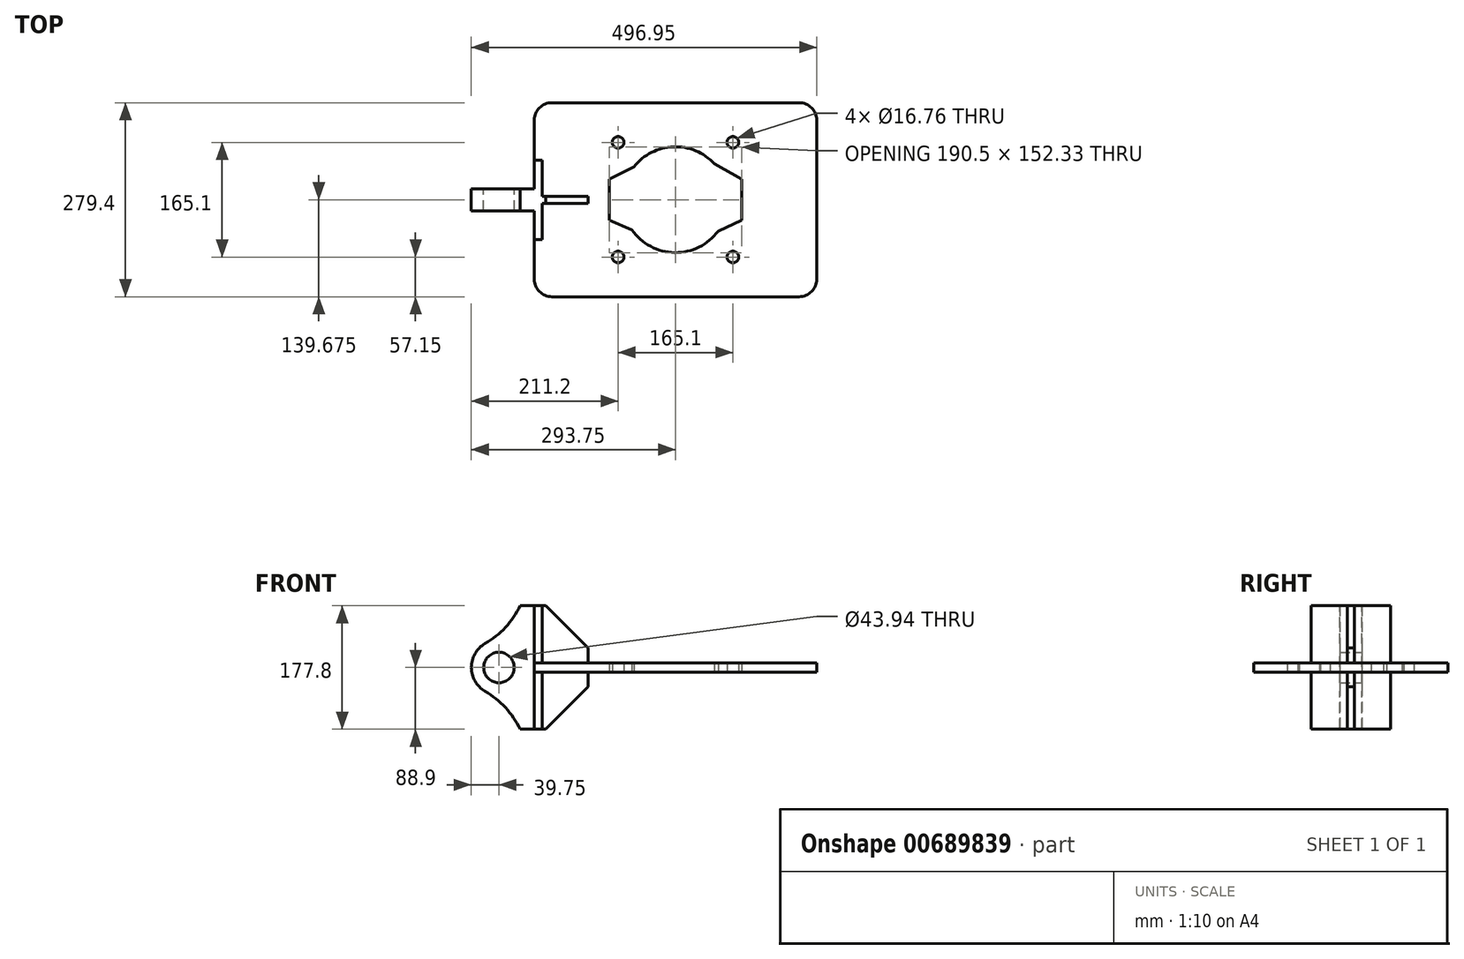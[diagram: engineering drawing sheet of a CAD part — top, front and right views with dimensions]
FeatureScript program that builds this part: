
annotation { "Feature Type Name" : "Feature", "Feature Type Description" : "" }
export const myFeature = defineFeature(function(context is Context, id is Id, definition is map)
    precondition{}
    {
        {
            var Q0;
            Q0=qCreatedBy(makeId("Top.planeOp"),FACE);
            var sketch = newSketch(context, id + "F0", { "sketchPlane" : qUnion([Q0])});
            skLineSegment(sketch, "E0.bottom", {"start": v(-177.8, 139.7) * mm, "end": v(177.8, 139.7) * mm});
            skLineSegment(sketch, "E0.top", {"start": v(-177.8, -139.7) * mm, "end": v(177.8, -139.7) * mm});
            skLineSegment(sketch, "E0.left", {"start": v(-203.2, 114.3) * mm, "end": v(-203.2, -114.3) * mm});
            skLineSegment(sketch, "E0.right", {"start": v(203.2, 114.3) * mm, "end": v(203.2, -114.3) * mm});
            skPoint(sketch, "E0.middle", {"position": v(0, 0) * mm});
            skLineSegment(sketch, "E1.bottom", {"start": v(-82.55, 82.55) * mm, "end": v(82.55, 82.55) * mm, "construction": true});
            skLineSegment(sketch, "E1.top", {"start": v(-82.55, -82.55) * mm, "end": v(82.55, -82.55) * mm, "construction": true});
            skLineSegment(sketch, "E1.left", {"start": v(-82.55, 82.55) * mm, "end": v(-82.55, -82.55) * mm, "construction": true});
            skLineSegment(sketch, "E1.right", {"start": v(82.55, 82.55) * mm, "end": v(82.55, -82.55) * mm, "construction": true});
            skCircle(sketch, "E2", {"center": v(-82.55, 82.55) * mm, "radius": 8.38 * mm});
            skCircle(sketch, "E3", {"center": v(82.55, 82.55) * mm, "radius": 8.38 * mm});
            skCircle(sketch, "E4", {"center": v(82.55, -82.55) * mm, "radius": 8.38 * mm});
            skCircle(sketch, "E5", {"center": v(-82.55, -82.55) * mm, "radius": 8.38 * mm});
            skPoint(sketch, "E6.visualSharp", {"position": v(-203.2, 139.7) * mm});
            skArc(sketch, "E6.filletArc", {"start": v(-177.8, 139.7) * mm, "mid": v(-195.76, 132.26) * mm, "end": v(-203.2, 114.3) * mm});
            skPoint(sketch, "E7.visualSharp", {"position": v(203.2, 139.7) * mm});
            skArc(sketch, "E7.filletArc", {"start": v(203.2, 114.3) * mm, "mid": v(195.76, 132.26) * mm, "end": v(177.8, 139.7) * mm});
            skPoint(sketch, "E8.visualSharp", {"position": v(-203.2, -139.7) * mm});
            skArc(sketch, "E8.filletArc", {"start": v(-203.2, -114.3) * mm, "mid": v(-195.76, -132.26) * mm, "end": v(-177.8, -139.7) * mm});
            skPoint(sketch, "E9.visualSharp", {"position": v(203.2, -139.7) * mm});
            skArc(sketch, "E9.filletArc", {"start": v(177.8, -139.7) * mm, "mid": v(195.76, -132.26) * mm, "end": v(203.2, -114.3) * mm});
            skSolve(sketch);
        }
        {
            var Q0;
            Q0 = qSketchRegion(id + "F0", true);
            extrude(context, id + "F1", {"entities" : qUnion([Q0]), "endBound" : BoundingType.SYMMETRIC, "depth" : 13.46 * mm, "offsetDistance" : 25.4 * mm});
        }
        {
            var Q0;
            Q0=makeQuery(id+"F1.opExtrude","SWEPT_FACE",FACE,{"disambiguationData":[OSD([sQuery(id+"F0.wireOp",EDGE,"E0.left")])]});
            var sketch = newSketch(context, id + "F2", { "sketchPlane" : qUnion([Q0])});
            skLineSegment(sketch, "E10.bottom", {"start": v(-57.15, 88.9) * mm, "end": v(57.15, 88.9) * mm});
            skLineSegment(sketch, "E10.top", {"start": v(-57.15, -88.9) * mm, "end": v(57.15, -88.9) * mm});
            skLineSegment(sketch, "E10.left", {"start": v(-57.15, 88.9) * mm, "end": v(-57.15, -88.9) * mm});
            skLineSegment(sketch, "E10.right", {"start": v(57.15, 88.9) * mm, "end": v(57.15, -88.9) * mm});
            skPoint(sketch, "E10.middle", {"position": v(0, 0) * mm});
            skSolve(sketch);
        }
        {
            var Q0;
            Q0 = qSketchRegion(id + "F2", true);
            extrude(context, id + "F3", {"entities" : qUnion([Q0]), "operationType" : NewBodyOperationType.ADD, "oppositeDirection" : true, "depth" : 11.33 * mm, "offsetDistance" : 25.4 * mm});
        }
        {
            var Q0;
            Q0=qCreatedBy(makeId("Front.planeOp"),FACE);
            var sketch = newSketch(context, id + "F4", { "sketchPlane" : qUnion([Q0])});
            skCircle(sketch, "E11", {"center": v(-254, 0) * mm, "radius": 21.97 * mm});
            skArc(sketch, "E12", {"start": v(-274, 34.35) * mm, "mid": v(-293.75, 0) * mm, "end": v(-274, -34.35) * mm});
            skLineSegment(sketch, "E13.0", {"start": v(-203.2, 88.9) * mm, "end": v(-203.2, 6.73) * mm});
            skLineSegment(sketch, "E13.1", {"start": v(-203.2, -6.73) * mm, "end": v(-203.2, -88.9) * mm});
            skLineSegment(sketch, "E14", {"start": v(-203.2, 88.9) * mm, "end": v(-223.52, 88.9) * mm});
            skLineSegment(sketch, "E15", {"start": v(-254, 0) * mm, "end": v(-203.2, 0) * mm, "construction": true});
            skLineSegment(sketch, "E16", {"start": v(-203.2, -6.73) * mm, "end": v(-203.2, 6.73) * mm});
            skArc(sketch, "E17", {"start": v(-274, 34.35) * mm, "mid": v(-244.68, 57.85) * mm, "end": v(-223.52, 88.9) * mm});
            skArc(sketch, "E18.MirrorCS", {"start": v(-274, -34.35) * mm, "mid": v(-244.68, -57.85) * mm, "end": v(-223.52, -88.9) * mm});
            skLineSegment(sketch, "E19.MirrorCS", {"start": v(-203.2, -88.9) * mm, "end": v(-223.52, -88.9) * mm});
            skSolve(sketch);
        }
        {
            var Q0;
            Q0 = qSketchRegion(id + "F4", true);
            extrude(context, id + "F5", {"entities" : qUnion([Q0]), "operationType" : NewBodyOperationType.ADD, "endBound" : BoundingType.SYMMETRIC, "depth" : 31.75 * mm, "offsetDistance" : 25.4 * mm});
        }
        {
            var Q0;
            Q0=makeQuery(id+"F5.boolean.opBoolean","MERGE",FACE,{"derivedFrom":[makeQuery(id+"F3.opExtrude","SWEPT_FACE",FACE,{"disambiguationData":[OSD([sQuery(id+"F2.wireOp",EDGE,"E10.bottom")])]}),makeQuery(id+"F5.opExtrude","SWEPT_FACE",FACE,{"disambiguationData":[OSD([sQuery(id+"F4.wireOp",EDGE,"E14")])]})]});
            var sketch = newSketch(context, id + "F6", { "sketchPlane" : qUnion([Q0])});
            skLineSegment(sketch, "E20.bottom", {"start": v(-191.87, 5.08) * mm, "end": v(-125.83, 5.08) * mm});
            skLineSegment(sketch, "E20.top", {"start": v(-191.87, -5.08) * mm, "end": v(-125.83, -5.08) * mm});
            skLineSegment(sketch, "E20.left", {"start": v(-191.87, 5.08) * mm, "end": v(-191.87, -5.08) * mm});
            skLineSegment(sketch, "E20.right", {"start": v(-125.83, 5.08) * mm, "end": v(-125.83, -5.08) * mm});
            skLineSegment(sketch, "E21", {"start": v(-125.83, 0) * mm, "end": v(0, 0) * mm, "construction": true});
            skSolve(sketch);
        }
        {
            var Q0;
            Q0 = qSketchRegion(id + "F6", true);
            var Q1;
            Q1=makeQuery(id+"F5.boolean.opBoolean","MERGE",FACE,{"derivedFrom":[makeQuery(id+"F3.opExtrude","SWEPT_FACE",FACE,{"disambiguationData":[OSD([sQuery(id+"F2.wireOp",EDGE,"E10.top")])]}),makeQuery(id+"F5.opExtrude","SWEPT_FACE",FACE,{"disambiguationData":[OSD([sQuery(id+"F4.wireOp",EDGE,"E19.MirrorCS")])]})]});
            extrude(context, id + "F7", {"entities" : qUnion([Q0]), "operationType" : NewBodyOperationType.ADD, "endBound" : BoundingType.UP_TO_SURFACE, "oppositeDirection" : true, "depth" : 25.4 * mm, "endBoundEntityFace" : qUnion([Q1]), "offsetDistance" : 25.4 * mm});
        }
        {
            var Q0;
            Q0=makeQuery(id+"F7.opExtrude","CAP_EDGE",EDGE,{"disambiguationData":[OSD([sQuery(id+"F6.wireOp",EDGE,"E20.right")])],"isStart":false});
            var Q1;
            Q1=makeQuery(id+"F7.opExtrude","CAP_EDGE",EDGE,{"disambiguationData":[OSD([sQuery(id+"F6.wireOp",EDGE,"E20.right")])],"isStart":true});
            chamfer(context, id + "F8", {"entities" : qUnion([Q0, Q1]), "width" : 60.96 * mm, "tangentPropagation" : true});
        }
        {
            var Q0;
            Q0=makeQuery(id+"F1.opExtrude","CAP_FACE",FACE,{"disambiguationData":[OSD([sQuery(id+"F0.wireOp",EDGE,"E0.bottom"),sQuery(id+"F0.wireOp",EDGE,"E0.top"),sQuery(id+"F0.wireOp",EDGE,"E0.left"),sQuery(id+"F0.wireOp",EDGE,"E0.right"),sQuery(id+"F0.wireOp",EDGE,"E2"),sQuery(id+"F0.wireOp",EDGE,"E3"),sQuery(id+"F0.wireOp",EDGE,"E4"),sQuery(id+"F0.wireOp",EDGE,"E5"),sQuery(id+"F0.wireOp",EDGE,"E6.filletArc"),sQuery(id+"F0.wireOp",EDGE,"E7.filletArc"),sQuery(id+"F0.wireOp",EDGE,"E8.filletArc"),sQuery(id+"F0.wireOp",EDGE,"E9.filletArc")])],"isStart":true});
            var sketch = newSketch(context, id + "F9", { "sketchPlane" : qUnion([Q0])});
            skArc(sketch, "E22", {"start": v(-59.66, -47.4) * mm, "mid": v(-2.96, -76.14) * mm, "end": v(55.8, -51.9) * mm});
            skLineSegment(sketch, "E23.left", {"start": v(-95.25, 29.53) * mm, "end": v(-95.25, -29.53) * mm});
            skLineSegment(sketch, "E23.right", {"start": v(95.25, 29.53) * mm, "end": v(95.25, -29.53) * mm});
            skLineSegment(sketch, "E24", {"start": v(-95.25, 29.53) * mm, "end": v(-62.67, 43.35) * mm});
            skLineSegment(sketch, "E25", {"start": v(-95.25, -29.53) * mm, "end": v(-59.66, -47.4) * mm});
            skLineSegment(sketch, "E26", {"start": v(95.25, -29.53) * mm, "end": v(55.8, -51.9) * mm});
            skLineSegment(sketch, "E27", {"start": v(95.25, 29.53) * mm, "end": v(61.4, 45.13) * mm});
            skArc(sketch, "E28.trimOffspring", {"start": v(61.4, 45.13) * mm, "mid": v(-1.1, 76.2) * mm, "end": v(-62.67, 43.35) * mm});
            skSolve(sketch);
        }
        {
            var Q0;
            Q0 = qSketchRegion(id + "F9", true);
            extrude(context, id + "F10", {"entities" : qUnion([Q0]), "operationType" : NewBodyOperationType.REMOVE, "endBound" : BoundingType.THROUGH_ALL, "oppositeDirection" : true, "depth" : 25.4 * mm, "offsetDistance" : 25.4 * mm});
        }
    });
